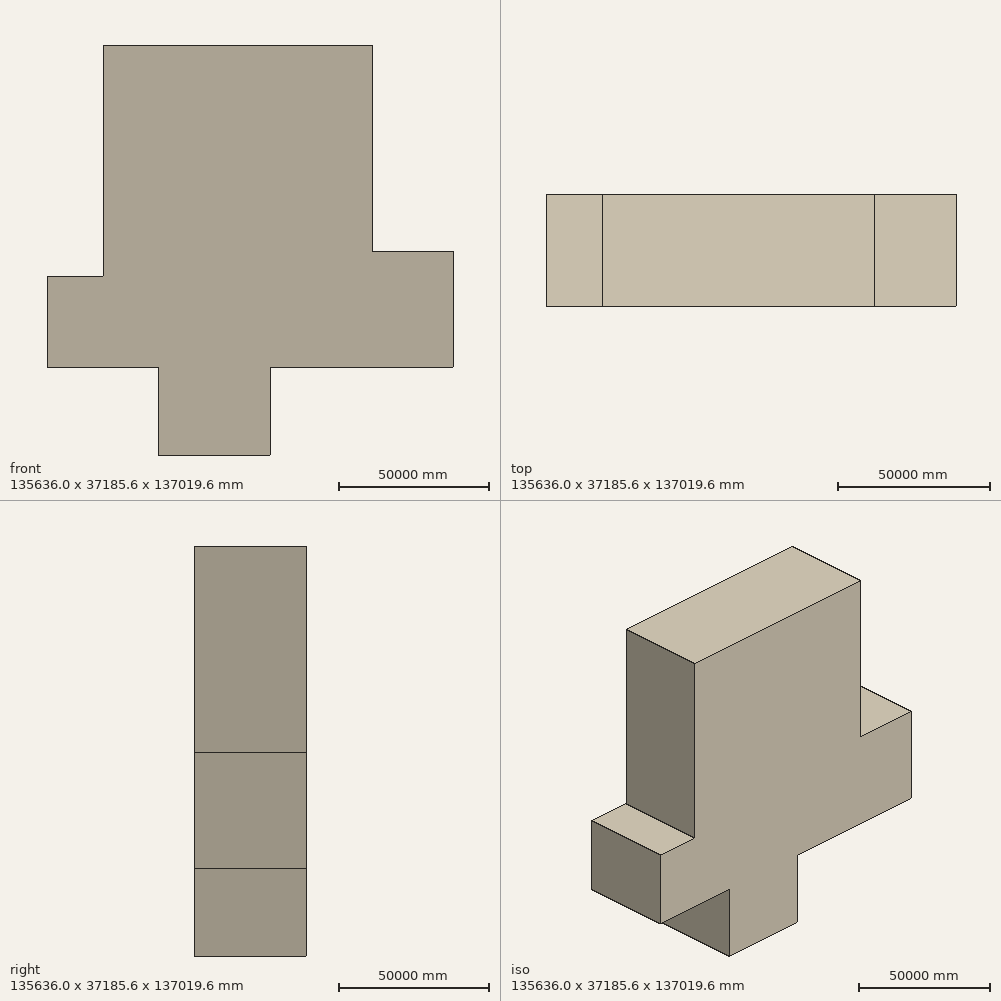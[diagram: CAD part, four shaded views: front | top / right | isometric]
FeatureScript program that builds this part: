
annotation { "Feature Type Name" : "Feature", "Feature Type Description" : "" }
export const myFeature = defineFeature(function(context is Context, id is Id, definition is map)
    precondition{}
    {
        {
            var Q0;
            Q0=qCreatedBy(makeId("Front.planeOp"),FACE);
            var sketch = newSketch(context, id + "F0", { "sketchPlane" : qUnion([Q0])});
            skLineSegment(sketch, "E0", {"start": v(0, 0) * mm, "end": v(37185.6, 0) * mm});
            skLineSegment(sketch, "E1", {"start": v(0, 0) * mm, "end": v(0, 30480) * mm});
            skLineSegment(sketch, "E2", {"start": v(0, 30480) * mm, "end": v(37185.6, 30480) * mm});
            skLineSegment(sketch, "E3", {"start": v(37185.6, -29483.34) * mm, "end": v(37185.6, 7702.26) * mm});
            skLineSegment(sketch, "E4", {"start": v(37185.6, 7702.26) * mm, "end": v(37185.6, 69112.77) * mm});
            skLineSegment(sketch, "E5", {"start": v(37185.6, 69112.77) * mm, "end": v(74371.2, 69112.77) * mm});
            skLineSegment(sketch, "E6", {"start": v(74371.2, 69112.77) * mm, "end": v(74371.2, -29483.34) * mm});
            skLineSegment(sketch, "E7", {"start": v(74371.2, -29483.34) * mm, "end": v(37185.6, -29483.34) * mm});
            skLineSegment(sketch, "E8", {"start": v(74371.2, 38663.97) * mm, "end": v(135636, 38663.97) * mm});
            skLineSegment(sketch, "E9", {"start": v(135636, 38663.97) * mm, "end": v(135636, 0) * mm});
            skLineSegment(sketch, "E10", {"start": v(135636, 0) * mm, "end": v(74371.2, 0) * mm});
            skLineSegment(sketch, "E11", {"start": v(18592.8, 30480) * mm, "end": v(18592.8, 107536.26) * mm});
            skLineSegment(sketch, "E12", {"start": v(18592.8, 107536.26) * mm, "end": v(108487.82, 107536.26) * mm});
            skLineSegment(sketch, "E13", {"start": v(108487.82, 107536.26) * mm, "end": v(108487.82, 38663.97) * mm});
            skSolve(sketch);
        }
        {
            var Q0;
            {var subQ2=sQuery(id+"F0.wireOp",EDGE,"E5");Q0=makeQuery(id+"F0.imprint","IMPRINT",FACE,{"disambiguationData":[TD([[makeQuery(id+"F0.imprint","IMPRINT",EDGE,{"derivedFrom":subQ2}),-1.0]])]});}
            var Q1;
            {var subQ0=sQuery(id+"F0.wireOp",EDGE,"E9");Q1=makeQuery(id+"F0.imprint","IMPRINT",FACE,{"disambiguationData":[TD([[makeQuery(id+"F0.imprint","IMPRINT",EDGE,{"derivedFrom":subQ0}),-1.0]])]});}
            var Q2;
            {var subQ1=sQuery(id+"F0.wireOp",EDGE,"E5");Q2=makeQuery(id+"F0.imprint","IMPRINT",FACE,{"disambiguationData":[TD([[makeQuery(id+"F0.imprint","IMPRINT",EDGE,{"derivedFrom":subQ1}),1.0]])]});}
            var Q3;
            {var subQ5=sQuery(id+"F0.wireOp",EDGE,"E0");Q3=makeQuery(id+"F0.imprint","IMPRINT",FACE,{"disambiguationData":[TD([[makeQuery(id+"F0.imprint","IMPRINT",EDGE,{"derivedFrom":subQ5}),1.0]])]});}
            extrude(context, id + "F1", {"entities" : qUnion([Q0, Q1, Q2, Q3]), "depth" : 37185.6 * mm, "offsetDistance" : 30.48 * mm});
        }
    });
